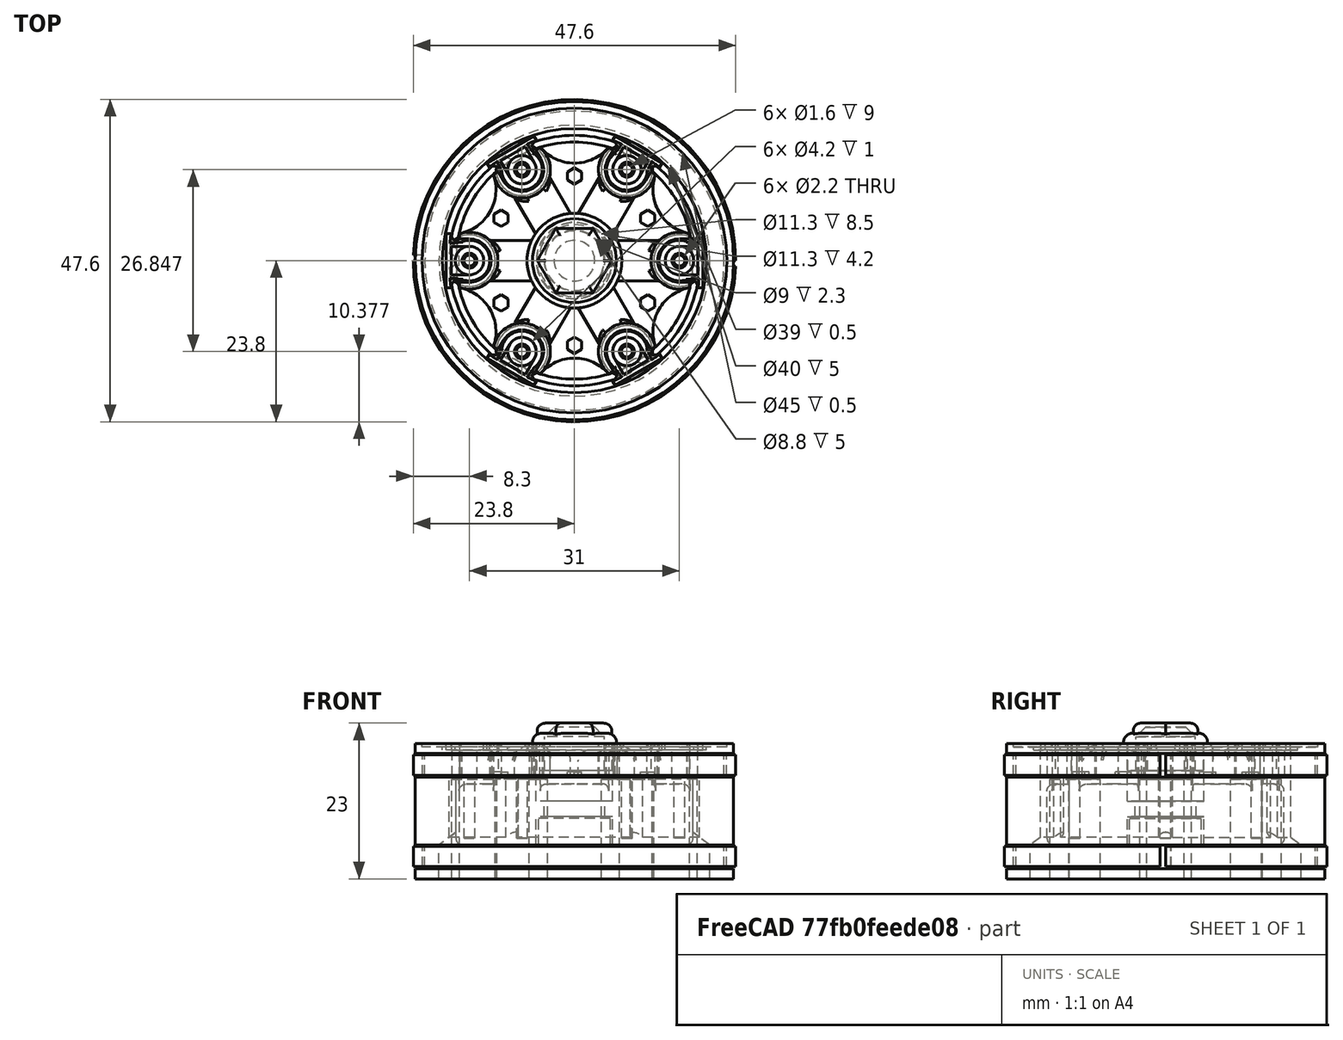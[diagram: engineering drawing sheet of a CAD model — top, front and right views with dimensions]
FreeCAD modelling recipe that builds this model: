
FCSTD DOCUMENT  (FreeCAD 0.15R4138 (Git))
Label: trilex_front_00
License: CC-BY 3.0
LicenseURL: http://creativecommons.org/licenses/by/3.0/
objects: Part::Cylinder×64, Part::Cut×29, Part::Fillet×28, Part::MultiFuse×26, Part::Feature×7, Part::Extrusion×7, Part::Box×6, Part::Cone×1, Part::Chamfer×1
note: 169 computed .brp shape members not serialized (recipe doc carries the construction recipe); baked Part::Feature solids carry a one-line shape summary decoded from their .brp

FEATURE [Part::Cylinder] Cylinder
  Angle = 360
  Height = 20
  Radius = 23.5
FEATURE [Part::Cylinder] Cylinder001
  Angle = 360
  Height = 17
  Radius = 23.5
FEATURE [Part::Cylinder] Cylinder002
  Angle = 360
  Height = 17
  Radius = 22.1
FEATURE [Part::Cut] Cut
  Base = -> Cylinder001
  Placement = pos=(0,0,1.5) rot=(0,0,1;0rad)
  Tool = -> Cylinder002
FEATURE [Part::Cut] Cut001
  Base = -> Cylinder
  Tool = -> Cut
FEATURE [Part::Cylinder] Cylinder003
  Angle = 360
  Height = 17
  Radius = 22
FEATURE [Part::Cylinder] Cylinder004
  Angle = 360
  Height = 10
  Placement = pos=(0,0,0.5) rot=(0,0,1;0rad)
  Radius = 23.5
FEATURE [Part::Cut] Cut002
  Base = -> Cylinder004
  Placement = pos=(0,0,4.5) rot=(0,0,1;0rad)
  Tool = -> Cylinder003
FEATURE [Part::Cylinder] Cylinder006
  Angle = 360
  Height = 20
  Radius = 18.5
FEATURE [Part::Cylinder] Cylinder007
  Angle = 360
  Height = 1
  Placement = pos=(0,0,19) rot=(0,0,1;0rad)
  Radius = 19.5
FEATURE [Part::Cylinder] Cylinder012
  Angle = 360
  Height = 5
  Placement = pos=(15.5,0,15) rot=(0,0,1;0rad)
  Radius = 3
FEATURE [Part::Box] Box  label="Cube"
  Height = 5
  Length = 2
  Placement = pos=(16.5,-2.75,15) rot=(0,0,1;0rad)
  Width = 5.5
FEATURE [Part::Cylinder] Cylinder018
  Angle = 360
  Height = 0.5
  Placement = pos=(0,0,19.5) rot=(0,0,1;0rad)
  Radius = 22.5
FEATURE [Part::Cylinder] Cylinder024
  Angle = 360
  Height = 10
  Placement = pos=(0,0,5) rot=(0,0,1;0rad)
  Radius = 17.5
FEATURE [Part::Cylinder] Cylinder025
  Angle = 360
  Height = 4.2
  Radius = 5.6
FEATURE [Part::Cylinder] Cylinder026
  Angle = 360
  Height = 10
  Placement = pos=(0,0,6.5) rot=(0,0,1;0rad)
  Radius = 5.6
FEATURE [Part::Cylinder] Cylinder027
  Angle = 360
  Height = 4
  Placement = pos=(0,0,3) rot=(0,0,1;0rad)
  Radius = 4.5
FEATURE [Part::MultiFuse] Fusion006
  Placement = pos=(0,0,5) rot=(0,0,1;0rad)
  Shapes = -> [Cylinder025,Cylinder026,Cylinder027]
FEATURE [Part::Cylinder] Cylinder028
  Angle = 360
  Height = 5
  Placement = pos=(0,0,15) rot=(0,0,1;0rad)
  Radius = 7
FEATURE [Part::MultiFuse] Fusion007
  Shapes = -> [Cylinder024,Cylinder028]
FEATURE [Part::Cylinder] Cylinder032
  Angle = 360
  Height = 15
  Placement = pos=(7.75,13.4234,6) rot=(0,0,1;1.0472rad)
  Radius = 0.8
FEATURE [Part::Box] Box005  label="Cube005"
  Height = 5
  Length = 16.5
  Placement = pos=(0,-3,14) rot=(0,0,1;0rad)
  Width = 6
FEATURE [Part::Cylinder] Cylinder041
  Angle = 360
  Height = 6
  Placement = pos=(15.5,0,14) rot=(0,0,1;0rad)
  Radius = 3.2
FEATURE [Part::Box] Box006  label="Cube006"
  Height = 6
  Length = 5
  Placement = pos=(15.5,-3.2,14) rot=(0,0,1;0rad)
  Width = 6.4
FEATURE [Part::Cylinder] Cylinder046
  Angle = 360
  Height = 10
  Placement = pos=(0,0,10) rot=(0,0,1;0rad)
  Radius = 5.6
FEATURE [Part::Cylinder] Cylinder047
  Angle = 360
  Height = 6
  Placement = pos=(15.5,0,14) rot=(0,0,1;0rad)
  Radius = 4.2
FEATURE [Part::Cylinder] Cylinder048
  Angle = 360
  Height = 6
  Placement = pos=(15.5,0,14) rot=(0,0,1;0rad)
  Radius = 3.2
FEATURE [Part::Cut] Cut016
  Base = -> Cylinder047
  Tool = -> Cylinder048
FEATURE [Part::Box] Box007  label="Cube007"
  Height = 6
  Length = 4
  Placement = pos=(17,-5,14) rot=(0,0,1;0rad)
  Width = 10
FEATURE [Part::MultiFuse] Fusion012
  Shapes = -> [Cylinder041,Box006]
FEATURE [Part::MultiFuse] Fusion013
  Shapes = -> [Cut016,Box005]
FEATURE [Part::Cut] Cut017
  Base = -> Fusion013
  Tool = -> Fusion012
FEATURE [Part::Cut] Cut018
  Base = -> Cut017
  Tool = -> Box007
FEATURE [Part::Cut] Cut019
  Base = -> Cut018
  Tool = -> Cylinder046
FEATURE [Part::Cut] Cut020
  Base = -> Fusion007
  Tool = -> Fusion006
FEATURE [Part::Cylinder] Cylinder049  label="hub-front-support"
  Angle = 360
  Height = 3.9
  Placement = pos=(0,0,5) rot=(0,0,1;0rad)
  Radius = 5.3
FEATURE [Part::Fillet] Fillet
  Base = -> Cut019
  Edges = 2 edges r=1.5: [Edge3,Edge22]
FEATURE [Part::Fillet] Fillet024
  Base = -> Fillet
  Edges = 1 edges r=0.4: [Edge10]
FEATURE [Part::Fillet] Fillet025
  Base = -> Fillet024
  Edges = 1 edges r=0.59: [Edge9]
  Placement = pos=(0,0,0) rot=(0,0,1;1.0472rad)
FEATURE [Part::Fillet] Fillet027
  Base = -> Fillet
  Edges = 1 edges r=0.4: [Edge10]
FEATURE [Part::Fillet] Fillet026
  Base = -> Fillet027
  Edges = 1 edges r=0.59: [Edge9]
  Placement = pos=(0,0,0) rot=(0,0,1;2.0944rad)
FEATURE [Part::Fillet] Fillet029
  Base = -> Fillet
  Edges = 1 edges r=0.4: [Edge10]
FEATURE [Part::Fillet] Fillet028
  Base = -> Fillet029
  Edges = 1 edges r=0.59: [Edge9]
  Placement = pos=(0,0,0) rot=(0,0,1;3.14159rad)
FEATURE [Part::Fillet] Fillet030
  Base = -> Fillet
  Edges = 1 edges r=0.4: [Edge10]
FEATURE [Part::Fillet] Fillet031
  Base = -> Fillet030
  Edges = 1 edges r=0.59: [Edge9]
  Placement = pos=(0,0,0) rot=(0,0,1;4.18879rad)
FEATURE [Part::Fillet] Fillet033
  Base = -> Fillet
  Edges = 1 edges r=0.4: [Edge10]
FEATURE [Part::Fillet] Fillet032
  Base = -> Fillet033
  Edges = 1 edges r=0.59: [Edge9]
  Placement = pos=(0,0,0) rot=(0,0,-1;1.0472rad)
FEATURE [Part::Fillet] Fillet034
  Base = -> Fillet
  Edges = 1 edges r=0.4: [Edge10]
FEATURE [Part::Fillet] Fillet035
  Base = -> Fillet034
  Edges = 1 edges r=0.59: [Edge9]
FEATURE [Part::MultiFuse] Fusion020
  Shapes = -> [Fillet025,Fillet032,Fillet028,Fillet026,Fillet031,Fillet035]
FEATURE [Part::Cylinder] Cylinder057
  Angle = 360
  Height = 15
  Placement = pos=(-7.75,13.4234,6) rot=(0,0,1;2.0944rad)
  Radius = 0.8
FEATURE [Part::Cylinder] Cylinder058
  Angle = 360
  Height = 15
  Placement = pos=(-15.5,0,6) rot=(0,0,1;3.14159rad)
  Radius = 0.8
FEATURE [Part::Cylinder] Cylinder059
  Angle = 360
  Height = 15
  Placement = pos=(-7.75,-13.4234,6) rot=(0,0,1;4.18879rad)
  Radius = 0.8
FEATURE [Part::Cylinder] Cylinder060
  Angle = 360
  Height = 15
  Placement = pos=(7.75,-13.4234,6) rot=(0,0,-1;1.0472rad)
  Radius = 0.8
FEATURE [Part::Cylinder] Cylinder061
  Angle = 360
  Height = 15
  Placement = pos=(15.5,0,6) rot=(0,0,1;0rad)
  Radius = 0.8
FEATURE [Part::MultiFuse] Fusion021
  Shapes = -> [Cylinder032,Cylinder060,Cylinder059,Cylinder061,Cylinder058,Cylinder057]
FEATURE [Part::Cylinder] Cylinder062
  Angle = 360
  Height = 1
  Placement = pos=(0,-21,14) rot=(0,0,1;1.5708rad)
  Radius = 6.6
FEATURE [Part::Cylinder] Cylinder063
  Angle = 360
  Height = 1
  Placement = pos=(18.1865,-10.5,14) rot=(0,0,1;2.61799rad)
  Radius = 6.6
FEATURE [Part::Cylinder] Cylinder064
  Angle = 360
  Height = 1
  Placement = pos=(18.1865,10.5,14) rot=(0,0,1;3.66519rad)
  Radius = 6.6
FEATURE [Part::Cylinder] Cylinder065
  Angle = 360
  Height = 1
  Placement = pos=(0,21,14) rot=(0,0,-1;1.5708rad)
  Radius = 6.6
FEATURE [Part::Cylinder] Cylinder066
  Angle = 360
  Height = 1
  Placement = pos=(-18.1865,10.5,14) rot=(0,0,-1;0.523599rad)
  Radius = 6.6
FEATURE [Part::Cylinder] Cylinder067
  Angle = 360
  Height = 1
  Placement = pos=(-18.1865,-10.5,14) rot=(0,0,1;0.523599rad)
  Radius = 6.6
FEATURE [Part::MultiFuse] Fusion022
  Shapes = -> [Cylinder062,Cylinder065,Cylinder064,Cylinder063,Cylinder066,Cylinder067]
FEATURE [Part::Cut] Cut027
  Base = -> Cut020
  Tool = -> Fusion022
FEATURE [Part::Cut] Cut028
  Base = -> Cut027
  Tool = -> Fusion021
FEATURE [Part::Fillet] Fillet036
  Base = -> Cut028
  Edges = 8 edges r=1: [Edge2,Edge5,Edge9,Edge13,Edge17,Edge21,Edge25,Edge69]
FEATURE [Part::MultiFuse] Fusion023  label="hub-front_00"
  Shapes = -> [Fusion020,Fillet036]
FEATURE [Part::Cylinder] Cylinder068
  Angle = 360
  Height = 5
  Placement = pos=(15.5,0,15) rot=(0,0,1;0rad)
  Radius = 1.1
FEATURE [Part::Box] Box010  label="Cube010"
  Height = 5
  Length = 0.75
  Placement = pos=(18.2,-4,15) rot=(0,0,1;0rad)
  Width = 8
FEATURE [Part::Cylinder] Cylinder069
  Angle = 360
  Height = 1
  Placement = pos=(15.5,0,19) rot=(0,0,1;0rad)
  Radius = 2.1
FEATURE [Part::MultiFuse] Fusion024
  Shapes = -> [Box,Box010,Cylinder012]
FEATURE [Part::MultiFuse] Fusion025
  Shapes = -> [Cylinder068,Cylinder069]
FEATURE [Part::Cut] Cut029
  Base = -> Fusion024
  Tool = -> Fusion025
FEATURE [Part::Box] Box011  label="Cube011"
  Height = 0.5
  Length = 2.7
  Placement = pos=(15.5,-2.1,19.5) rot=(0,0,1;0rad)
  Width = 4.2
FEATURE [Part::Cut] Cut030
  Base = -> Cut029
  Tool = -> Box011
FEATURE [Part::Fillet] Fillet047
  Base = -> Cut030
  Edges = 8 edges r=0.2: [Edge1,Edge5,Edge6,Edge7,Edge8,Edge9,Edge10,Edge11]
FEATURE [Part::Fillet] Fillet048
  Base = -> Fillet047
  Edges = 2 edges r=1.2: [Edge1,Edge39]
  Placement = pos=(0,0,0) rot=(0,0,1;1.0472rad)
FEATURE [Part::Fillet] Fillet049
  Base = -> Cut030
  Edges = 8 edges r=0.2: [Edge1,Edge5,Edge6,Edge7,Edge8,Edge9,Edge10,Edge11]
FEATURE [Part::Fillet] Fillet050
  Base = -> Fillet049
  Edges = 2 edges r=1.2: [Edge1,Edge39]
  Placement = pos=(0,0,0) rot=(0,0,1;2.0944rad)
FEATURE [Part::Fillet] Fillet051
  Base = -> Cut030
  Edges = 8 edges r=0.2: [Edge1,Edge5,Edge6,Edge7,Edge8,Edge9,Edge10,Edge11]
FEATURE [Part::Fillet] Fillet052
  Base = -> Fillet051
  Edges = 2 edges r=1.2: [Edge1,Edge39]
  Placement = pos=(0,0,0) rot=(0,0,1;3.14159rad)
FEATURE [Part::Fillet] Fillet053
  Base = -> Cut030
  Edges = 8 edges r=0.2: [Edge1,Edge5,Edge6,Edge7,Edge8,Edge9,Edge10,Edge11]
FEATURE [Part::Fillet] Fillet054
  Base = -> Fillet053
  Edges = 2 edges r=1.2: [Edge1,Edge39]
  Placement = pos=(0,0,0) rot=(0,0,1;4.18879rad)
FEATURE [Part::Fillet] Fillet055
  Base = -> Cut030
  Edges = 8 edges r=0.2: [Edge1,Edge5,Edge6,Edge7,Edge8,Edge9,Edge10,Edge11]
FEATURE [Part::Fillet] Fillet056
  Base = -> Fillet055
  Edges = 2 edges r=1.2: [Edge1,Edge39]
  Placement = pos=(0,0,0) rot=(0,0,-1;1.0472rad)
FEATURE [Part::Fillet] Fillet057
  Base = -> Cut030
  Edges = 8 edges r=0.2: [Edge1,Edge5,Edge6,Edge7,Edge8,Edge9,Edge10,Edge11]
FEATURE [Part::Fillet] Fillet058
  Base = -> Fillet057
  Edges = 2 edges r=1.2: [Edge1,Edge39]
FEATURE [Part::MultiFuse] Fusion026  label="rim-holes"
  Shapes = -> [Fillet048,Fillet050,Fillet058,Fillet052,Fillet056,Fillet054]
FEATURE [Part::Feature] Face
  shape: bbox 2.85 x 2.65 x 2e-07 mm, 1 faces, 0 solids (baked)
FEATURE [Part::Extrusion] Extrude
  Base = -> Face
  Dir = (0,0,2)
  Placement = pos=(10.8253,6.25,13.8) rot=(0,0,1;0.523599rad)
  Solid = false
FEATURE [Part::Feature] Face001
  shape: bbox 2.85 x 2.65 x 2e-07 mm, 1 faces, 0 solids (baked)
FEATURE [Part::Extrusion] Extrude001
  Base = -> Face001
  Dir = (0,0,2)
  Placement = pos=(0,12.5,13.8) rot=(0,0,1;1.5708rad)
  Solid = false
FEATURE [Part::Feature] Face002
  shape: bbox 2.85 x 2.65 x 2e-07 mm, 1 faces, 0 solids (baked)
FEATURE [Part::Extrusion] Extrude002
  Base = -> Face002
  Dir = (0,0,2)
  Placement = pos=(-10.8253,6.25,13.8) rot=(0,0,1;2.61799rad)
  Solid = false
FEATURE [Part::Feature] Face003
  shape: bbox 2.85 x 2.65 x 2e-07 mm, 1 faces, 0 solids (baked)
FEATURE [Part::Extrusion] Extrude003
  Base = -> Face003
  Dir = (0,0,2)
  Placement = pos=(-10.8253,-6.25,13.8) rot=(0,0,1;3.66519rad)
  Solid = false
FEATURE [Part::Feature] Face004
  shape: bbox 2.85 x 2.65 x 2e-07 mm, 1 faces, 0 solids (baked)
FEATURE [Part::Extrusion] Extrude004
  Base = -> Face004
  Dir = (0,0,2)
  Placement = pos=(0,-12.5,13.8) rot=(0,0,-1;1.5708rad)
  Solid = false
FEATURE [Part::Feature] Face005
  shape: bbox 2.85 x 2.65 x 2e-07 mm, 1 faces, 0 solids (baked)
FEATURE [Part::Extrusion] Extrude005
  Base = -> Face005
  Dir = (0,0,2)
  Placement = pos=(10.8253,-6.25,13.8) rot=(0,0,-1;0.523599rad)
  Solid = false
FEATURE [Part::MultiFuse] Fusion028
  Shapes = -> [Extrude,Extrude001,Extrude004,Extrude002,Extrude005,Extrude003]
FEATURE [Part::MultiFuse] Fusion029  label="hub-front_001"
  Shapes = -> [Fusion023,Fusion028]
FEATURE [Part::Cylinder] Cylinder070
  Angle = 360
  Height = 5
  Radius = 20
FEATURE [Part::Cylinder] Cylinder071
  Angle = 360
  Height = 10
  Placement = pos=(18.5,0,5) rot=(0,0,1;0rad)
  Radius = 1
FEATURE [Part::Cylinder] Cylinder072
  Angle = 360
  Height = 10
  Placement = pos=(9.25,16.0215,5) rot=(0,0,1;1.0472rad)
  Radius = 1
FEATURE [Part::Cylinder] Cylinder073
  Angle = 360
  Height = 10
  Placement = pos=(-9.25,16.0215,5) rot=(0,0,1;2.0944rad)
  Radius = 1
FEATURE [Part::Cylinder] Cylinder074
  Angle = 360
  Height = 10
  Placement = pos=(-18.5,0,5) rot=(0,0,1;3.14159rad)
  Radius = 1
FEATURE [Part::Cylinder] Cylinder075
  Angle = 360
  Height = 10
  Placement = pos=(-9.25,-16.0215,5) rot=(0,0,1;4.18879rad)
  Radius = 1
FEATURE [Part::Cylinder] Cylinder076
  Angle = 360
  Height = 10
  Placement = pos=(9.25,-16.0215,5) rot=(0,0,-1;1.0472rad)
  Radius = 1
FEATURE [Part::MultiFuse] Fusion030
  Shapes = -> [Cylinder071,Cylinder073,Cylinder075,Cylinder072,Cylinder074,Cylinder076]
FEATURE [Part::MultiFuse] Fusion
  Shapes = -> [Cut002,Cut001]
FEATURE [Part::Cut] Cut031
  Base = -> Fusion
  Tool = -> Cylinder006
FEATURE [Part::Cut] Cut032
  Base = -> Cut031
  Tool = -> Cylinder018
FEATURE [Part::Cut] Cut033
  Base = -> Cut032
  Tool = -> Cylinder007
FEATURE [Part::Cut] Cut034
  Base = -> Cut033
  Tool = -> Cylinder070
FEATURE [Part::Cylinder] Cylinder078
  Angle = 178
  Height = 3
  Placement = pos=(0,0,1.8) rot=(0,0,1;0rad)
  Radius = 23.8
FEATURE [Part::Cylinder] Cylinder079
  Angle = 360
  Height = 17
  Radius = 22.45
FEATURE [Part::Cut] Cut035
  Base = -> Cylinder078
  Tool = -> Cylinder079
FEATURE [Part::Cylinder] Cylinder080
  Angle = 178
  Height = 3
  Placement = pos=(0,0,1.8) rot=(0,0,1;0rad)
  Radius = 23.8
FEATURE [Part::Cylinder] Cylinder081
  Angle = 360
  Height = 17
  Radius = 22.45
FEATURE [Part::Cut] Cut036
  Base = -> Cylinder080
  Placement = pos=(0,0,0) rot=(0,0,1;3.14159rad)
  Tool = -> Cylinder081
FEATURE [Part::MultiFuse] Fusion032
  Placement = pos=(0,0,13.5) rot=(0,0,1;0rad)
  Shapes = -> [Cut035,Cut036]
FEATURE [Part::Cut] Cut037
  Base = -> Cylinder080
  Placement = pos=(0,0,0) rot=(0,0,1;3.14159rad)
  Tool = -> Cylinder081
FEATURE [Part::Cut] Cut038
  Base = -> Cylinder078
  Tool = -> Cylinder079
FEATURE [Part::MultiFuse] Fusion033
  Shapes = -> [Cut038,Cut037]
FEATURE [Part::MultiFuse] Fusion034
  Shapes = -> [Fusion032,Fusion033]
FEATURE [Part::Cylinder] Cylinder082
  Angle = 360
  Height = 4.2
  Radius = 5.65
FEATURE [Part::Cylinder] Cylinder083
  Angle = 360
  Height = 10
  Placement = pos=(0,0,6.5) rot=(0,0,1;0rad)
  Radius = 5.65
FEATURE [Part::Cylinder] Cylinder084
  Angle = 360
  Height = 4
  Placement = pos=(0,0,3) rot=(0,0,1;0rad)
  Radius = 4.5
FEATURE [Part::MultiFuse] Fusion035
  Placement = pos=(0,0,5) rot=(0,0,1;0rad)
  Shapes = -> [Cylinder082,Cylinder084,Cylinder083]
FEATURE [Part::Cut] Cut039  label="hub-front"
  Base = -> Fusion029
  Tool = -> Fusion035
FEATURE [Part::MultiFuse] Fusion036
  Shapes = -> [Cut034,Fusion030]
FEATURE [Part::MultiFuse] Fusion037  label="rim-front_00"
  Shapes = -> [Fusion026,Fusion036]
FEATURE [Part::Cylinder] Cylinder085
  Angle = 360
  Height = 14.7
  Placement = pos=(15.5,0,0) rot=(0,0,1;0rad)
  Radius = 3.8
FEATURE [Part::Cylinder] Cylinder086
  Angle = 360
  Height = 15
  Placement = pos=(21,0,0) rot=(0,0,1;0rad)
  Radius = 4
FEATURE [Part::Cut] Cut051
  Base = -> Cylinder085
  Placement = pos=(0,0,0) rot=(0,0,1;1.0472rad)
  Tool = -> Cylinder086
FEATURE [Part::Cylinder] Cylinder087
  Angle = 360
  Height = 14.7
  Placement = pos=(15.5,0,0) rot=(0,0,1;0rad)
  Radius = 3.8
FEATURE [Part::Cylinder] Cylinder088
  Angle = 360
  Height = 15
  Placement = pos=(21,0,0) rot=(0,0,1;0rad)
  Radius = 4
FEATURE [Part::Cut] Cut052
  Base = -> Cylinder087
  Placement = pos=(0,0,0) rot=(0,0,1;2.0944rad)
  Tool = -> Cylinder088
FEATURE [Part::Cylinder] Cylinder089
  Angle = 360
  Height = 14.7
  Placement = pos=(15.5,0,0) rot=(0,0,1;0rad)
  Radius = 3.8
FEATURE [Part::Cylinder] Cylinder090
  Angle = 360
  Height = 15
  Placement = pos=(21,0,0) rot=(0,0,1;0rad)
  Radius = 4
FEATURE [Part::Cut] Cut053
  Base = -> Cylinder089
  Placement = pos=(0,0,0) rot=(0,0,1;3.14159rad)
  Tool = -> Cylinder090
FEATURE [Part::Cylinder] Cylinder091
  Angle = 360
  Height = 14.7
  Placement = pos=(15.5,0,0) rot=(0,0,1;0rad)
  Radius = 3.8
FEATURE [Part::Cylinder] Cylinder092
  Angle = 360
  Height = 15
  Placement = pos=(21,0,0) rot=(0,0,1;0rad)
  Radius = 4
FEATURE [Part::Cut] Cut054
  Base = -> Cylinder091
  Placement = pos=(0,0,0) rot=(0,0,1;4.18879rad)
  Tool = -> Cylinder092
FEATURE [Part::Cylinder] Cylinder093
  Angle = 360
  Height = 14.7
  Placement = pos=(15.5,0,0) rot=(0,0,1;0rad)
  Radius = 3.8
FEATURE [Part::Cylinder] Cylinder094
  Angle = 360
  Height = 15
  Placement = pos=(21,0,0) rot=(0,0,1;0rad)
  Radius = 4
FEATURE [Part::Cut] Cut055
  Base = -> Cylinder093
  Placement = pos=(0,0,0) rot=(0,0,-1;1.0472rad)
  Tool = -> Cylinder094
FEATURE [Part::Cylinder] Cylinder095
  Angle = 360
  Height = 14.7
  Placement = pos=(15.5,0,0) rot=(0,0,1;0rad)
  Radius = 3.8
FEATURE [Part::Cylinder] Cylinder096
  Angle = 360
  Height = 15
  Placement = pos=(21,0,0) rot=(0,0,1;0rad)
  Radius = 4
FEATURE [Part::Cut] Cut056
  Base = -> Cylinder095
  Tool = -> Cylinder096
FEATURE [Part::MultiFuse] Fusion038
  Shapes = -> [Cut051,Cut054,Cut055,Cut053,Cut052,Cut056]
FEATURE [Part::MultiFuse] Fusion039  label="rim-front-support"
  Shapes = -> [Fusion038,Fusion034]
FEATURE [Part::Cone] Cone
  Angle = 360
  Height = 6
  Placement = pos=(0,0,5) rot=(0,0,1;0rad)
  Radius1 = 20
  Radius2 = 12
FEATURE [Part::Cut] Cut057  label="rim-front"
  Base = -> Fusion037
  Tool = -> Cone
FEATURE [Part::Cylinder] Cylinder098
  Angle = 360
  Height = 11
  Placement = pos=(0,0,12) rot=(0,0,1;0rad)
  Radius = 4.4
FEATURE [Part::Cylinder] Cylinder097
  Angle = 360
  Height = 8.6
  Placement = pos=(0,0,11.5) rot=(0,0,1;0rad)
  Radius = 5.575
FEATURE [Part::Cylinder] Cylinder099
  Angle = 360
  Height = 1.5
  Placement = pos=(0,0,20) rot=(0,0,1;0rad)
  Radius = 6.2
FEATURE [Part::Cylinder] Cylinder100
  Angle = 360
  Height = 5
  Placement = pos=(0,0,11) rot=(0,0,1;0rad)
  Radius = 6
FEATURE [Part::MultiFuse] Fusion041
  Shapes = -> [Cylinder098,Cylinder100]
FEATURE [Part::Chamfer] Chamfer001
  Base = -> Fusion041
  Edges = 1 edges r=2: [Edge1]
FEATURE [Part::Feature] Face007
  shape: bbox 16.53 x 16.53 x 2e-07 mm, 1 faces, 0 solids (baked)
FEATURE [Part::Extrusion] Extrude008
  Base = -> Face007
  Dir = (0,0,2)
  Placement = pos=(0,0,-4) rot=(0,0,1;0rad)
  Solid = false
FEATURE [Part::Fillet] Fillet059
  Base = -> Cylinder099
  Edges = 1 edges r=1.3: [Edge1]
FEATURE [Part::Fillet] Fillet060
  Base = -> Extrude008
  Edges = 6 edges r=1.1: [Edge4,Edge7,Edge10,Edge13,Edge16,Edge18]
FEATURE [Part::MultiFuse] Fusion042
  Shapes = -> [Cylinder097,Fillet059,Fillet060]
FEATURE [Part::Cut] Cut058
  Base = -> Fusion042
  Tool = -> Chamfer001
FEATURE [Part::Cylinder] Cylinder101
  Angle = 360
  Height = 0.6
  Placement = pos=(0,0,22.4) rot=(0,0,1;0rad)
  Radius = 3.5
FEATURE [Part::MultiFuse] Fusion043  label="front-cap"
  Shapes = -> [Cylinder101,Cut058]
